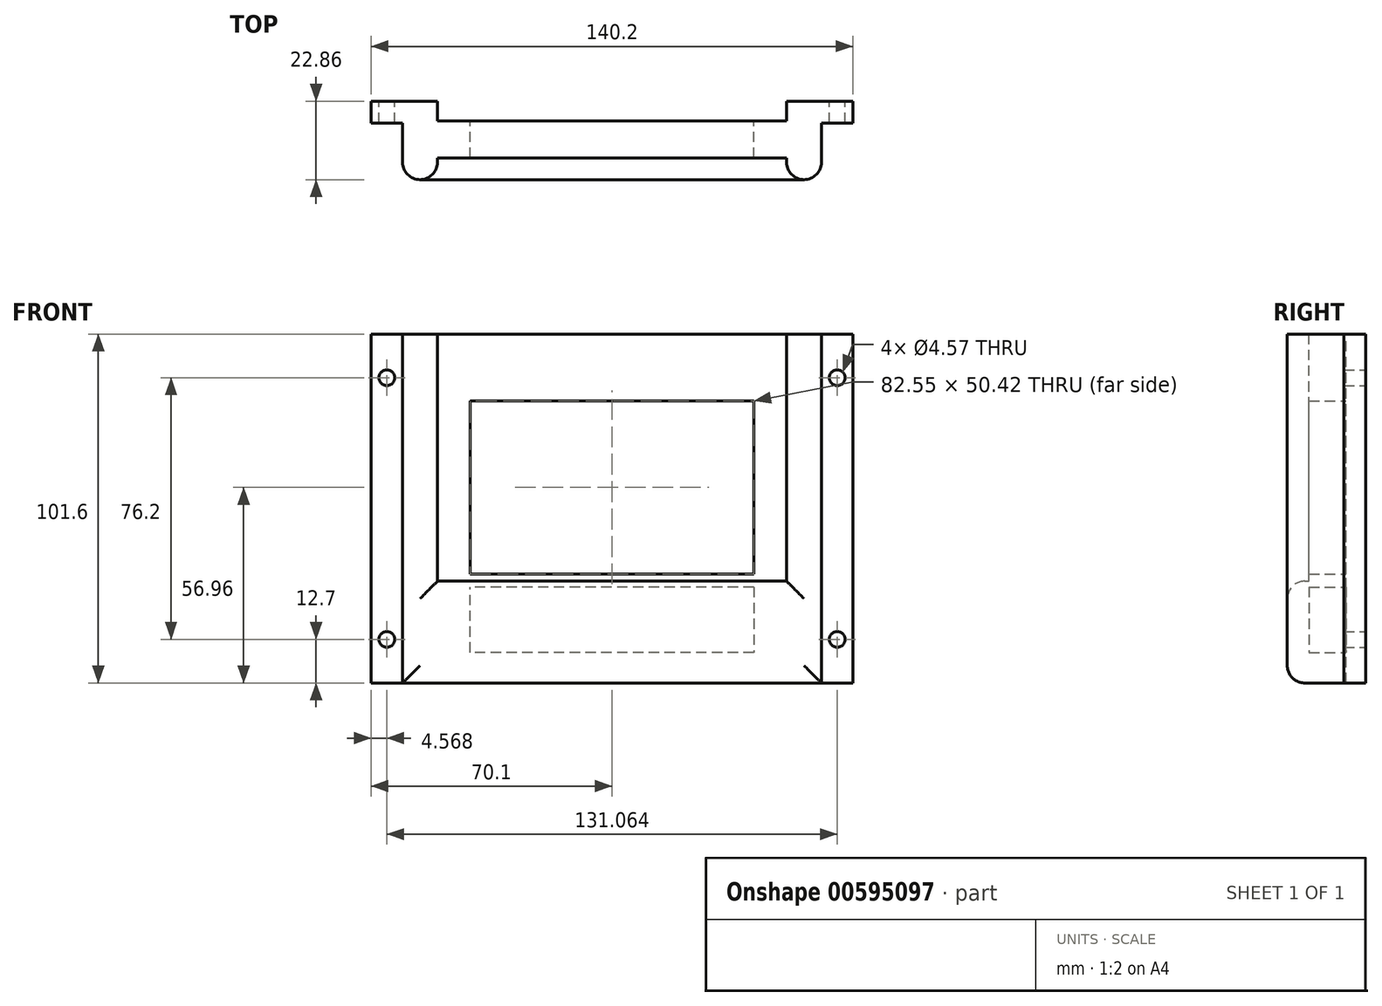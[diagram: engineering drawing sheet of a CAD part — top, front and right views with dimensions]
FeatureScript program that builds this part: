
annotation { "Feature Type Name" : "Feature", "Feature Type Description" : "" }
export const myFeature = defineFeature(function(context is Context, id is Id, definition is map)
    precondition{}
    {
        {
            var Q0;
            Q0=qCreatedBy(makeId("Front.planeOp"),FACE);
            var sketch = newSketch(context, id + "F0", { "sketchPlane" : qUnion([Q0])});
            skLineSegment(sketch, "E0.bottom", {"start": v(41.28, -25.2) * mm, "end": v(-41.28, -25.2) * mm});
            skLineSegment(sketch, "E0.top", {"start": v(41.27, 25.2) * mm, "end": v(-41.28, 25.2) * mm});
            skLineSegment(sketch, "E0.left", {"start": v(41.28, -25.2) * mm, "end": v(41.27, 25.2) * mm});
            skLineSegment(sketch, "E0.right", {"start": v(-41.27, -25.2) * mm, "end": v(-41.28, 25.2) * mm});
            skPoint(sketch, "E0.middle", {"position": v(0, 0) * mm});
            skLineSegment(sketch, "E1.bottom", {"start": v(50.8, -56.96) * mm, "end": v(-50.8, -56.96) * mm});
            skLineSegment(sketch, "E1.left", {"start": v(50.8, -56.96) * mm, "end": v(50.8, 44.64) * mm});
            skLineSegment(sketch, "E1.right", {"start": v(-50.8, -56.96) * mm, "end": v(-50.8, 44.64) * mm});
            skLineSegment(sketch, "E2", {"start": v(0, -29.02) * mm, "end": v(-41.28, -29.02) * mm});
            skLineSegment(sketch, "E3", {"start": v(0, -29.02) * mm, "end": v(41.28, -29.02) * mm});
            skLineSegment(sketch, "E4", {"start": v(41.28, -29.02) * mm, "end": v(41.28, -48.07) * mm});
            skLineSegment(sketch, "E5", {"start": v(41.28, -48.07) * mm, "end": v(-41.28, -48.07) * mm});
            skLineSegment(sketch, "E6", {"start": v(-41.28, -48.07) * mm, "end": v(-41.28, -29.02) * mm});
            skLineSegment(sketch, "E7", {"start": v(-50.8, 44.64) * mm, "end": v(50.8, 44.64) * mm});
            skSolve(sketch);
        }
        {
            var Q0;
            Q0=makeQuery(id+"F0.imprint","IMPRINT",FACE,{"disambiguationData":[TD([[makeQuery(id+"F0.imprint","IMPRINT",EDGE,{"derivedFrom":sQuery(id+"F0.wireOp",EDGE,"E0.bottom")}),1.0]])]});
            extrude(context, id + "F1", {"entities" : qUnion([Q0]), "depth" : 10.8 * mm, "offsetDistance" : 25.4 * mm});
        }
        {
            var Q0;
            Q0=makeQuery(id+"F1.opExtrude","CAP_FACE",FACE,{"disambiguationData":[OSD([sQuery(id+"F0.wireOp",EDGE,"E0.bottom"),sQuery(id+"F0.wireOp",EDGE,"E0.top"),sQuery(id+"F0.wireOp",EDGE,"E0.left"),sQuery(id+"F0.wireOp",EDGE,"E0.right"),sQuery(id+"F0.wireOp",EDGE,"E1.bottom"),sQuery(id+"F0.wireOp",EDGE,"E1.left"),sQuery(id+"F0.wireOp",EDGE,"E1.right"),sQuery(id+"F0.wireOp",EDGE,"E2"),sQuery(id+"F0.wireOp",EDGE,"E3"),sQuery(id+"F0.wireOp",EDGE,"E4"),sQuery(id+"F0.wireOp",EDGE,"E5"),sQuery(id+"F0.wireOp",EDGE,"E6"),sQuery(id+"F0.wireOp",EDGE,"E7")])],"isStart":false});
            var sketch = newSketch(context, id + "F2", { "sketchPlane" : qUnion([Q0])});
            skLineSegment(sketch, "E8", {"start": v(-50.8, -27.3) * mm, "end": v(-50.8, -56.96) * mm});
            skLineSegment(sketch, "E9", {"start": v(-50.8, -56.96) * mm, "end": v(50.8, -56.96) * mm});
            skLineSegment(sketch, "E10", {"start": v(50.8, -56.96) * mm, "end": v(50.8, -27.3) * mm});
            skLineSegment(sketch, "E11", {"start": v(-50.8, -27.3) * mm, "end": v(50.8, -27.3) * mm});
            skSolve(sketch);
        }
        {
            var Q0;
            {var subQ0=sQuery(id+"F2.wireOp",EDGE,"E8");Q0=makeQuery(id+"F2.imprint","IMPRINT",FACE,{"disambiguationData":[TD([[makeQuery(id+"F2.imprint","IMPRINT",EDGE,{"derivedFrom":subQ0}),-1.0]])]});}
            var Q1;
            Q1=makeQuery(id+"F2.imprint","IMPRINT",FACE,{"disambiguationData":[TD([[makeQuery(id+"F2.imprint","IMPRINT",EDGE,{"derivedFrom":makeQuery(id+"F1.opExtrude","CAP_EDGE",EDGE,{"disambiguationData":[OSD([sQuery(id+"F0.wireOp",EDGE,"E4")])],"isStart":false})}),-1.0]])]});
            extrude(context, id + "F3", {"entities" : qUnion([Q0, Q1]), "operationType" : NewBodyOperationType.ADD, "depth" : 6.35 * mm, "offsetDistance" : 25.4 * mm});
        }
        {
            var Q0;
            Q0=makeQuery(id+"F3.opExtrude","CAP_FACE",FACE,{"disambiguationData":[OSD([sQuery(id+"F2.wireOp",EDGE,"E8"),sQuery(id+"F2.wireOp",EDGE,"E9"),sQuery(id+"F2.wireOp",EDGE,"E10"),sQuery(id+"F2.wireOp",EDGE,"E11")])],"isStart":false});
            var sketch = newSketch(context, id + "F4", { "sketchPlane" : qUnion([Q0])});
            skLineSegment(sketch, "E12", {"start": v(-50.8, -56.96) * mm, "end": v(-50.8, 44.64) * mm});
            skLineSegment(sketch, "E13", {"start": v(50.8, 44.64) * mm, "end": v(50.8, -56.96) * mm});
            skLineSegment(sketch, "E14", {"start": v(-50.8, 44.64) * mm, "end": v(-60.96, 44.64) * mm});
            skLineSegment(sketch, "E15", {"start": v(-60.96, 44.64) * mm, "end": v(-60.96, -56.96) * mm});
            skLineSegment(sketch, "E16", {"start": v(-60.96, -56.96) * mm, "end": v(-50.8, -56.96) * mm});
            skLineSegment(sketch, "E17", {"start": v(50.8, 44.64) * mm, "end": v(60.96, 44.64) * mm});
            skLineSegment(sketch, "E18", {"start": v(60.96, 44.64) * mm, "end": v(60.96, -56.96) * mm});
            skLineSegment(sketch, "E19", {"start": v(60.96, -56.96) * mm, "end": v(50.8, -56.96) * mm});
            skSolve(sketch);
        }
        {
            var Q0;
            Q0 = qSketchRegion(id + "F4", true);
            extrude(context, id + "F5", {"entities" : qUnion([Q0]), "operationType" : NewBodyOperationType.ADD, "oppositeDirection" : true, "depth" : 22.86 * mm, "offsetDistance" : 25.4 * mm});
        }
        {
            var Q0;
            Q0=makeQuery(id+"F5.opExtrude","CAP_FACE",FACE,{"disambiguationData":[OSD([sQuery(id+"F4.wireOp",EDGE,"E13"),sQuery(id+"F4.wireOp",EDGE,"E17"),sQuery(id+"F4.wireOp",EDGE,"E18"),sQuery(id+"F4.wireOp",EDGE,"E19")])],"isStart":false});
            var sketch = newSketch(context, id + "F6", { "sketchPlane" : qUnion([Q0])});
            skLineSegment(sketch, "E20", {"start": v(-60.96, -56.96) * mm, "end": v(-70.1, -56.96) * mm});
            skLineSegment(sketch, "E21", {"start": v(-70.1, -56.96) * mm, "end": v(-70.1, 44.64) * mm});
            skLineSegment(sketch, "E22", {"start": v(-70.1, 44.64) * mm, "end": v(-60.96, 44.64) * mm});
            skLineSegment(sketch, "E23", {"start": v(-60.96, 44.64) * mm, "end": v(-60.96, -56.96) * mm});
            skCircle(sketch, "E24", {"center": v(-65.53, -44.26) * mm, "radius": 2.29 * mm});
            skCircle(sketch, "E25", {"center": v(-65.53, 31.94) * mm, "radius": 2.29 * mm});
            skLineSegment(sketch, "E26.MirrorCS", {"start": v(60.96, 44.64) * mm, "end": v(60.96, -56.96) * mm});
            skLineSegment(sketch, "E27.MirrorCS", {"start": v(70.1, -56.96) * mm, "end": v(70.1, 44.64) * mm});
            skLineSegment(sketch, "E28.MirrorCS", {"start": v(60.96, -56.96) * mm, "end": v(70.1, -56.96) * mm});
            skLineSegment(sketch, "E29.MirrorCS", {"start": v(70.1, 44.64) * mm, "end": v(60.96, 44.64) * mm});
            skCircle(sketch, "E30.MirrorC", {"center": v(65.53, 31.94) * mm, "radius": 2.29 * mm});
            skCircle(sketch, "E31.MirrorC", {"center": v(65.53, -44.26) * mm, "radius": 2.29 * mm});
            skSolve(sketch);
        }
        {
            var Q0;
            Q0 = qSketchRegion(id + "F6", true);
            extrude(context, id + "F7", {"entities" : qUnion([Q0]), "operationType" : NewBodyOperationType.ADD, "oppositeDirection" : true, "depth" : 6.35 * mm, "offsetDistance" : 25.4 * mm});
        }
        {
            var Q0;
            Q0=makeQuery(id+"F5.opExtrude","CAP_EDGE",EDGE,{"disambiguationData":[OSD([sQuery(id+"F4.wireOp",EDGE,"E15")])],"isStart":true});
            var Q1;
            Q1=makeQuery(id+"F5.boolean.opBoolean","MERGE",EDGE,{"derivedFrom":[makeQuery(id+"F3.opExtrude","CAP_EDGE",EDGE,{"disambiguationData":[OSD([sQuery(id+"F2.wireOp",EDGE,"E9")])],"isStart":false}),makeQuery(id+"F5.opExtrude","CAP_EDGE",EDGE,{"disambiguationData":[OSD([sQuery(id+"F4.wireOp",EDGE,"E16")])],"isStart":true}),makeQuery(id+"F5.opExtrude","CAP_EDGE",EDGE,{"disambiguationData":[OSD([sQuery(id+"F4.wireOp",EDGE,"E19")])],"isStart":true})]});
            var Q2;
            Q2=makeQuery(id+"F5.opExtrude","CAP_EDGE",EDGE,{"disambiguationData":[OSD([sQuery(id+"F4.wireOp",EDGE,"E18")])],"isStart":true});
            fillet(context, id + "F8", {"entities" : qUnion([Q0, Q1, Q2]), "radius" : 5.08 * mm, "tangentPropagation" : true, "allowEdgeOverflow" : false});
        }
        {
            var Q0;
            Q0=makeQuery(id+"F5.opExtrude","CAP_EDGE",EDGE,{"disambiguationData":[OSD([sQuery(id+"F4.wireOp",EDGE,"E12")])],"isStart":true});
            var Q1;
            Q1=makeQuery(id+"F3.opExtrude","CAP_EDGE",EDGE,{"disambiguationData":[OSD([sQuery(id+"F2.wireOp",EDGE,"E11")])],"isStart":false});
            var Q2;
            Q2=makeQuery(id+"F5.opExtrude","CAP_EDGE",EDGE,{"disambiguationData":[OSD([sQuery(id+"F4.wireOp",EDGE,"E13")])],"isStart":true});
            fillet(context, id + "F9", {"entities" : qUnion([Q0, Q1, Q2]), "radius" : 5.08 * mm, "tangentPropagation" : true, "allowEdgeOverflow" : false});
        }
    });
